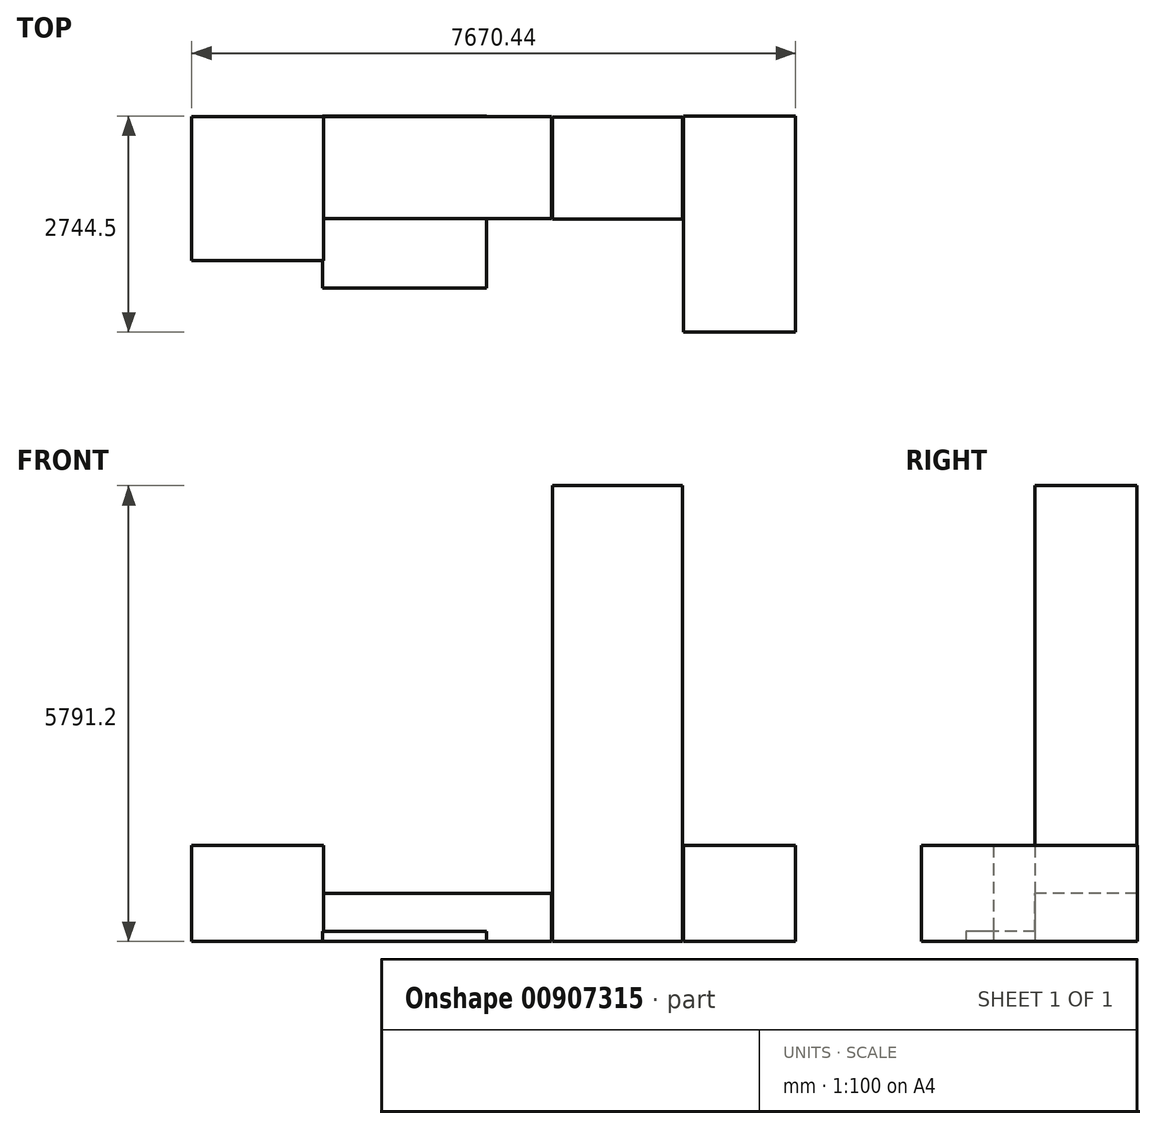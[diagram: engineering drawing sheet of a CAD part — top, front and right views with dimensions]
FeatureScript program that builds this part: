
annotation { "Feature Type Name" : "Feature", "Feature Type Description" : "" }
export const myFeature = defineFeature(function(context is Context, id is Id, definition is map)
    precondition{}
    {
        {
            var Q0;
            Q0=qCreatedBy(makeId("Top.planeOp"),FACE);
            var sketch = newSketch(context, id + "F0", { "sketchPlane" : qUnion([Q0])});
            skLineSegment(sketch, "E0.bottom", {"start": v(-3817.32, 5193.99) * mm, "end": v(3828.08, 5193.99) * mm});
            skLineSegment(sketch, "E0.top", {"start": v(-3817.32, -3645.21) * mm, "end": v(3828.08, -3645.21) * mm});
            skLineSegment(sketch, "E0.left", {"start": v(-3817.32, 5193.99) * mm, "end": v(-3817.32, -3645.21) * mm});
            skLineSegment(sketch, "E0.right", {"start": v(3828.08, 5193.99) * mm, "end": v(3828.08, -3645.21) * mm});
            skSolve(sketch);
        }
        {
            var Q0;
            Q0=makeQuery(id+"F0.imprint","IMPRINT",FACE,{"disambiguationData":[TD([[makeQuery(id+"F0.imprint","IMPRINT",EDGE,{"derivedFrom":sQuery(id+"F0.wireOp",EDGE,"E0.bottom")}),-1.0]])]});
            var sketch = newSketch(context, id + "F1", { "sketchPlane" : qUnion([Q0])});
            skLineSegment(sketch, "E1.bottom", {"start": v(-3838.58, 5193.9) * mm, "end": v(-2162.18, 5193.9) * mm});
            skLineSegment(sketch, "E1.top", {"start": v(-3838.58, 3365.1) * mm, "end": v(-2162.18, 3365.1) * mm});
            skLineSegment(sketch, "E1.left", {"start": v(-3838.58, 5193.9) * mm, "end": v(-3838.58, 3365.1) * mm});
            skLineSegment(sketch, "E1.right", {"start": v(-2162.18, 5193.9) * mm, "end": v(-2162.18, 3365.1) * mm});
            skSolve(sketch);
        }
        {
            var Q0;
            {var subQ0=sQuery(id+"F1.wireOp",EDGE,"E1.left");Q0=makeQuery(id+"F1.imprint","IMPRINT",FACE,{"disambiguationData":[TD([[makeQuery(id+"F1.imprint","IMPRINT",EDGE,{"derivedFrom":subQ0}),1.0]])]});}
            var Q1;
            {var subQ0=sQuery(id+"F1.wireOp",EDGE,"E1.right");Q1=makeQuery(id+"F1.imprint","IMPRINT",FACE,{"disambiguationData":[TD([[makeQuery(id+"F1.imprint","IMPRINT",EDGE,{"derivedFrom":subQ0}),-1.0]])]});}
            extrude(context, id + "F2", {"entities" : qUnion([Q0, Q1]), "depth" : 1219.2 * mm, "offsetDistance" : 25.4 * mm});
        }
        {
            var Q0;
            Q0=makeQuery(id+"F0.imprint","IMPRINT",FACE,{"disambiguationData":[TD([[makeQuery(id+"F0.imprint","IMPRINT",EDGE,{"derivedFrom":sQuery(id+"F0.wireOp",EDGE,"E0.bottom")}),-1.0]])]});
            var sketch = newSketch(context, id + "F3", { "sketchPlane" : qUnion([Q0])});
            skLineSegment(sketch, "E2.bottom", {"start": v(-2164.82, 5190.03) * mm, "end": v(730.78, 5190.03) * mm});
            skLineSegment(sketch, "E2.top", {"start": v(-2164.82, 3894.63) * mm, "end": v(730.78, 3894.63) * mm});
            skLineSegment(sketch, "E2.left", {"start": v(-2164.82, 5190.03) * mm, "end": v(-2164.82, 3894.63) * mm});
            skLineSegment(sketch, "E2.right", {"start": v(730.78, 5190.03) * mm, "end": v(730.78, 3894.63) * mm});
            skSolve(sketch);
        }
        {
            var Q0;
            Q0=makeQuery(id+"F0.imprint","IMPRINT",FACE,{"disambiguationData":[TD([[makeQuery(id+"F0.imprint","IMPRINT",EDGE,{"derivedFrom":sQuery(id+"F0.wireOp",EDGE,"E0.bottom")}),-1.0]])]});
            var sketch = newSketch(context, id + "F4", { "sketchPlane" : qUnion([Q0])});
            skLineSegment(sketch, "E3.bottom", {"start": v(742.1, 5185.47) * mm, "end": v(2393.1, 5185.47) * mm});
            skLineSegment(sketch, "E3.top", {"start": v(742.1, 3890.07) * mm, "end": v(2393.1, 3890.07) * mm});
            skLineSegment(sketch, "E3.left", {"start": v(742.1, 5185.47) * mm, "end": v(742.1, 3890.07) * mm});
            skLineSegment(sketch, "E3.right", {"start": v(2393.1, 5185.47) * mm, "end": v(2393.1, 3890.07) * mm});
            skSolve(sketch);
        }
        {
            var Q0;
            Q0 = qSketchRegion(id + "F4", true);
            extrude(context, id + "F5", {"entities" : qUnion([Q0]), "depth" : 5791.2 * mm, "offsetDistance" : 25.4 * mm});
        }
        {
            var Q0;
            Q0 = qSketchRegion(id + "F3", true);
            extrude(context, id + "F6", {"entities" : qUnion([Q0]), "operationType" : NewBodyOperationType.ADD, "depth" : 609.6 * mm, "offsetDistance" : 25.4 * mm});
        }
        {
            var Q0;
            Q0=makeQuery(id+"F0.imprint","IMPRINT",FACE,{"disambiguationData":[TD([[makeQuery(id+"F0.imprint","IMPRINT",EDGE,{"derivedFrom":sQuery(id+"F0.wireOp",EDGE,"E0.bottom")}),-1.0]])]});
            var sketch = newSketch(context, id + "F7", { "sketchPlane" : qUnion([Q0])});
            skLineSegment(sketch, "E4.bottom", {"start": v(3831.86, 5196.6) * mm, "end": v(2409.46, 5196.6) * mm});
            skLineSegment(sketch, "E4.top", {"start": v(3831.86, 2453.4) * mm, "end": v(2409.46, 2453.4) * mm});
            skLineSegment(sketch, "E4.left", {"start": v(3831.86, 5196.6) * mm, "end": v(3831.86, 2453.4) * mm});
            skLineSegment(sketch, "E4.right", {"start": v(2409.46, 5196.6) * mm, "end": v(2409.46, 2453.4) * mm});
            skSolve(sketch);
        }
        {
            var Q0;
            Q0 = qSketchRegion(id + "F7", true);
            extrude(context, id + "F8", {"entities" : qUnion([Q0]), "depth" : 1219.2 * mm, "offsetDistance" : 25.4 * mm});
        }
        {
            var Q0;
            Q0=makeQuery(id+"F3.imprint","IMPRINT",FACE,{"disambiguationData":[TD([[makeQuery(id+"F3.imprint","IMPRINT",EDGE,{"derivedFrom":sQuery(id+"F3.wireOp",EDGE,"E2.bottom")}),1.0]])]});
            var sketch = newSketch(context, id + "F9", { "sketchPlane" : qUnion([Q0])});
            skLineSegment(sketch, "E5.bottom", {"start": v(-2178.68, 5197.9) * mm, "end": v(-95.88, 5197.9) * mm});
            skLineSegment(sketch, "E5.top", {"start": v(-2178.68, 3013.5) * mm, "end": v(-95.88, 3013.5) * mm});
            skLineSegment(sketch, "E5.left", {"start": v(-2178.68, 5197.9) * mm, "end": v(-2178.68, 3013.5) * mm});
            skLineSegment(sketch, "E5.right", {"start": v(-95.88, 5197.9) * mm, "end": v(-95.88, 3013.5) * mm});
            skSolve(sketch);
        }
        {
            var Q0;
            Q0 = qSketchRegion(id + "F9", true);
            extrude(context, id + "F10", {"entities" : qUnion([Q0]), "operationType" : NewBodyOperationType.ADD, "depth" : 127 * mm, "offsetDistance" : 25.4 * mm});
        }
    });
